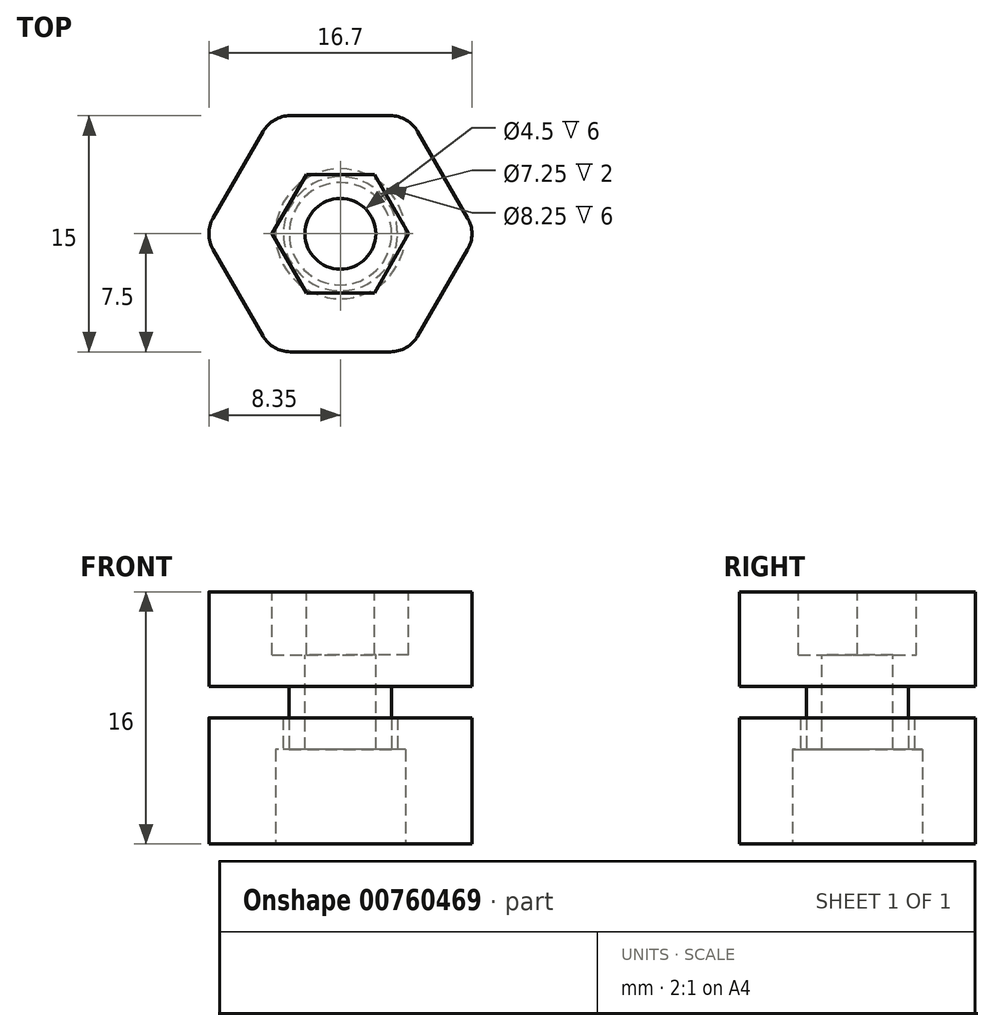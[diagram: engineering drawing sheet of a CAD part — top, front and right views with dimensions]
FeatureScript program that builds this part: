
annotation { "Feature Type Name" : "Feature", "Feature Type Description" : "" }
export const myFeature = defineFeature(function(context is Context, id is Id, definition is map)
    precondition{}
    {
        {
            var Q0;
            Q0=qCreatedBy(makeId("Top.planeOp"),FACE);
            var sketch = newSketch(context, id + "F0", { "sketchPlane" : qUnion([Q0])});
            skCircle(sketch, "E0", {"center": v(0, 0) * mm, "radius": 4.12 * mm});
            skCircle(sketch, "E1", {"center": v(0, 0) * mm, "radius": 3.62 * mm});
            skCircle(sketch, "E2.cCircle", {"center": v(0, 0) * mm, "radius": 7.5 * mm, "construction": true});
            skLineSegment(sketch, "E2.0", {"start": v(-4.33, 7.5) * mm, "end": v(4.33, 7.5) * mm});
            skLineSegment(sketch, "E2.1", {"start": v(4.33, 7.5) * mm, "end": v(8.66, 0) * mm});
            skLineSegment(sketch, "E2.2", {"start": v(8.66, 0) * mm, "end": v(4.33, -7.5) * mm});
            skLineSegment(sketch, "E2.3", {"start": v(4.33, -7.5) * mm, "end": v(-4.33, -7.5) * mm});
            skLineSegment(sketch, "E2.4", {"start": v(-4.33, -7.5) * mm, "end": v(-8.66, 0) * mm});
            skLineSegment(sketch, "E2.5", {"start": v(-8.66, 0) * mm, "end": v(-4.33, 7.5) * mm});
            skPoint(sketch, "E2.0.midPoint", {"position": v(0, 7.5) * mm});
            skSolve(sketch);
        }
        {
            var Q0;
            Q0=makeQuery(id+"F0.imprint","IMPRINT",FACE,{"disambiguationData":[TD([[makeQuery(id+"F0.imprint","IMPRINT",EDGE,{"derivedFrom":sQuery(id+"F0.wireOp",EDGE,"E0")}),-1.0]])]});
            var Q1;
            Q1=makeQuery(id+"F0.imprint","IMPRINT",FACE,{"disambiguationData":[TD([[makeQuery(id+"F0.imprint","IMPRINT",EDGE,{"derivedFrom":sQuery(id+"F0.wireOp",EDGE,"E0")}),1.0]])]});
            extrude(context, id + "F1", {"entities" : qUnion([Q0, Q1]), "depth" : 8 * mm, "offsetDistance" : 25 * mm});
        }
        {
            var Q0;
            Q0=makeQuery(id+"F0.imprint","IMPRINT",FACE,{"disambiguationData":[TD([[makeQuery(id+"F0.imprint","IMPRINT",EDGE,{"derivedFrom":sQuery(id+"F0.wireOp",EDGE,"E0")}),1.0]])]});
            extrude(context, id + "F2", {"entities" : qUnion([Q0]), "operationType" : NewBodyOperationType.REMOVE, "depth" : 6 * mm, "offsetDistance" : 25 * mm});
        }
        {
            var Q0;
            Q0=makeQuery(id+"F2.boolean.opBoolean","COPY",FACE,{"derivedFrom":makeQuery(id+"F2.opExtrude","CAP_FACE",FACE,{"disambiguationData":[OSD([sQuery(id+"F0.wireOp",EDGE,"E0"),sQuery(id+"F0.wireOp",EDGE,"E1")])],"isStart":false})});
            var sketch = newSketch(context, id + "F3", { "sketchPlane" : qUnion([Q0])});
            skCircle(sketch, "E3", {"center": v(0, 0) * mm, "radius": 3.25 * mm});
            skSolve(sketch);
        }
        {
            var Q0;
            Q0=makeQuery(id+"F3.imprint","IMPRINT",FACE,{"disambiguationData":[TD([[makeQuery(id+"F3.imprint","IMPRINT",EDGE,{"derivedFrom":sQuery(id+"F3.wireOp",EDGE,"E3")}),1.0]])]});
            extrude(context, id + "F4", {"entities" : qUnion([Q0]), "oppositeDirection" : true, "depth" : 4 * mm, "offsetDistance" : 25 * mm});
        }
        {
            var Q0;
            Q0=makeQuery(id+"F4.opExtrude","CAP_FACE",FACE,{"disambiguationData":[OSD([sQuery(id+"F3.wireOp",EDGE,"E3"),sQuery(id+"F3.wireOp",EDGE,"KjZoWoZm-BD7A-KjsF-ZKL1-DKTP2S4fCj8n")])],"isStart":false});
            var sketch = newSketch(context, id + "F5", { "sketchPlane" : qUnion([Q0])});
            skCircle(sketch, "E4.cCircle", {"center": v(0, 0) * mm, "radius": 7.5 * mm, "construction": true});
            skLineSegment(sketch, "E4.0", {"start": v(-4.33, 7.5) * mm, "end": v(4.33, 7.5) * mm});
            skLineSegment(sketch, "E4.1", {"start": v(4.33, 7.5) * mm, "end": v(8.66, 0) * mm});
            skLineSegment(sketch, "E4.2", {"start": v(8.66, 0) * mm, "end": v(4.33, -7.5) * mm});
            skLineSegment(sketch, "E4.3", {"start": v(4.33, -7.5) * mm, "end": v(-4.33, -7.5) * mm});
            skLineSegment(sketch, "E4.4", {"start": v(-4.33, -7.5) * mm, "end": v(-8.66, 0) * mm});
            skLineSegment(sketch, "E4.5", {"start": v(-8.66, 0) * mm, "end": v(-4.33, 7.5) * mm});
            skPoint(sketch, "E4.0.midPoint", {"position": v(0, 7.5) * mm});
            skSolve(sketch);
        }
        {
            var Q0;
            Q0=makeQuery(id+"F5.imprint","IMPRINT",FACE,{"disambiguationData":[TD([[makeQuery(id+"F5.imprint","IMPRINT",EDGE,{"derivedFrom":sQuery(id+"F5.wireOp",EDGE,"E4.0")}),-1.0]])]});
            var Q1;
            Q1=makeQuery(id+"F5.imprint","IMPRINT",FACE,{"disambiguationData":[TD([[makeQuery(id+"F5.imprint","IMPRINT",EDGE,{"derivedFrom":makeQuery(id+"F4.opExtrude","CAP_EDGE",EDGE,{"disambiguationData":[OSD([sQuery(id+"F3.wireOp",EDGE,"E3")])],"isStart":false})}),-1.0]])]});
            extrude(context, id + "F6", {"entities" : qUnion([Q0, Q1]), "operationType" : NewBodyOperationType.ADD, "depth" : 6 * mm, "offsetDistance" : 25 * mm});
        }
        {
            var Q0;
            Q0=makeQuery(id+"F6.opExtrude","CAP_FACE",FACE,{"disambiguationData":[OSD([sQuery(id+"F5.wireOp",EDGE,"E4.0"),sQuery(id+"F5.wireOp",EDGE,"E4.1"),sQuery(id+"F5.wireOp",EDGE,"E4.2"),sQuery(id+"F5.wireOp",EDGE,"E4.3"),sQuery(id+"F5.wireOp",EDGE,"E4.4"),sQuery(id+"F5.wireOp",EDGE,"E4.5")])],"isStart":false});
            var sketch = newSketch(context, id + "F7", { "sketchPlane" : qUnion([Q0])});
            skCircle(sketch, "E5", {"center": v(0, 0) * mm, "radius": 2.25 * mm});
            skCircle(sketch, "E6.cCircle", {"center": v(0, 0) * mm, "radius": 3.75 * mm, "construction": true});
            skLineSegment(sketch, "E6.0", {"start": v(-2.17, 3.75) * mm, "end": v(2.17, 3.75) * mm});
            skLineSegment(sketch, "E6.1", {"start": v(2.17, 3.75) * mm, "end": v(4.33, 0) * mm});
            skLineSegment(sketch, "E6.2", {"start": v(4.33, 0) * mm, "end": v(2.17, -3.75) * mm});
            skLineSegment(sketch, "E6.3", {"start": v(2.17, -3.75) * mm, "end": v(-2.17, -3.75) * mm});
            skLineSegment(sketch, "E6.4", {"start": v(-2.17, -3.75) * mm, "end": v(-4.33, 0) * mm});
            skLineSegment(sketch, "E6.5", {"start": v(-4.33, 0) * mm, "end": v(-2.17, 3.75) * mm});
            skPoint(sketch, "E6.0.midPoint", {"position": v(0, 3.75) * mm});
            skSolve(sketch);
        }
        {
            var Q0;
            Q0=makeQuery(id+"F7.imprint","IMPRINT",FACE,{"disambiguationData":[TD([[makeQuery(id+"F7.imprint","IMPRINT",EDGE,{"derivedFrom":sQuery(id+"F7.wireOp",EDGE,"E5")}),1.0]])]});
            extrude(context, id + "F8", {"entities" : qUnion([Q0]), "operationType" : NewBodyOperationType.REMOVE, "endBound" : BoundingType.THROUGH_ALL, "oppositeDirection" : true, "depth" : 25 * mm, "offsetDistance" : 25 * mm});
        }
        {
            var Q0;
            Q0=makeQuery(id+"F7.imprint","IMPRINT",FACE,{"disambiguationData":[TD([[makeQuery(id+"F7.imprint","IMPRINT",EDGE,{"derivedFrom":sQuery(id+"F7.wireOp",EDGE,"E5")}),-1.0]])]});
            extrude(context, id + "F9", {"entities" : qUnion([Q0]), "operationType" : NewBodyOperationType.REMOVE, "oppositeDirection" : true, "depth" : 4 * mm, "offsetDistance" : 25 * mm});
        }
        {
            var Q0;
            Q0=makeQuery(id+"F1.opExtrude","SWEPT_EDGE",EDGE,{"disambiguationData":[OSD([sQuery(id+"F0.wireOp",EDGE,"E2.4"),sQuery(id+"F0.wireOp",EDGE,"E2.5")])]});
            var Q1;
            Q1=makeQuery(id+"F6.opExtrude","SWEPT_EDGE",EDGE,{"disambiguationData":[OSD([sQuery(id+"F5.wireOp",EDGE,"E4.4"),sQuery(id+"F5.wireOp",EDGE,"E4.5")])]});
            var Q2;
            Q2=makeQuery(id+"F6.opExtrude","SWEPT_EDGE",EDGE,{"disambiguationData":[OSD([sQuery(id+"F5.wireOp",EDGE,"E4.0"),sQuery(id+"F5.wireOp",EDGE,"E4.5")])]});
            var Q3;
            Q3=makeQuery(id+"F1.opExtrude","SWEPT_EDGE",EDGE,{"disambiguationData":[OSD([sQuery(id+"F0.wireOp",EDGE,"E2.0"),sQuery(id+"F0.wireOp",EDGE,"E2.5")])]});
            var Q4;
            Q4=makeQuery(id+"F1.opExtrude","SWEPT_EDGE",EDGE,{"disambiguationData":[OSD([sQuery(id+"F0.wireOp",EDGE,"E2.3"),sQuery(id+"F0.wireOp",EDGE,"E2.4")])]});
            var Q5;
            Q5=makeQuery(id+"F6.opExtrude","SWEPT_EDGE",EDGE,{"disambiguationData":[OSD([sQuery(id+"F5.wireOp",EDGE,"E4.3"),sQuery(id+"F5.wireOp",EDGE,"E4.4")])]});
            var Q6;
            Q6=makeQuery(id+"F1.opExtrude","SWEPT_EDGE",EDGE,{"disambiguationData":[OSD([sQuery(id+"F0.wireOp",EDGE,"E2.2"),sQuery(id+"F0.wireOp",EDGE,"E2.3")])]});
            var Q7;
            Q7=makeQuery(id+"F1.opExtrude","SWEPT_EDGE",EDGE,{"disambiguationData":[OSD([sQuery(id+"F0.wireOp",EDGE,"E2.1"),sQuery(id+"F0.wireOp",EDGE,"E2.2")])]});
            var Q8;
            Q8=makeQuery(id+"F1.opExtrude","SWEPT_EDGE",EDGE,{"disambiguationData":[OSD([sQuery(id+"F0.wireOp",EDGE,"E2.0"),sQuery(id+"F0.wireOp",EDGE,"E2.1")])]});
            var Q9;
            Q9=makeQuery(id+"F6.opExtrude","SWEPT_EDGE",EDGE,{"disambiguationData":[OSD([sQuery(id+"F5.wireOp",EDGE,"E4.0"),sQuery(id+"F5.wireOp",EDGE,"E4.1")])]});
            var Q10;
            Q10=makeQuery(id+"F6.opExtrude","SWEPT_EDGE",EDGE,{"disambiguationData":[OSD([sQuery(id+"F5.wireOp",EDGE,"E4.1"),sQuery(id+"F5.wireOp",EDGE,"E4.2")])]});
            var Q11;
            Q11=makeQuery(id+"F6.opExtrude","SWEPT_EDGE",EDGE,{"disambiguationData":[OSD([sQuery(id+"F5.wireOp",EDGE,"E4.2"),sQuery(id+"F5.wireOp",EDGE,"E4.3")])]});
            fillet(context, id + "F10", {"entities" : qUnion([Q0, Q1, Q2, Q3, Q4, Q5, Q6, Q7, Q8, Q9, Q10, Q11]), "radius" : 2 * mm, "tangentPropagation" : true, "allowEdgeOverflow" : false});
        }
    });
